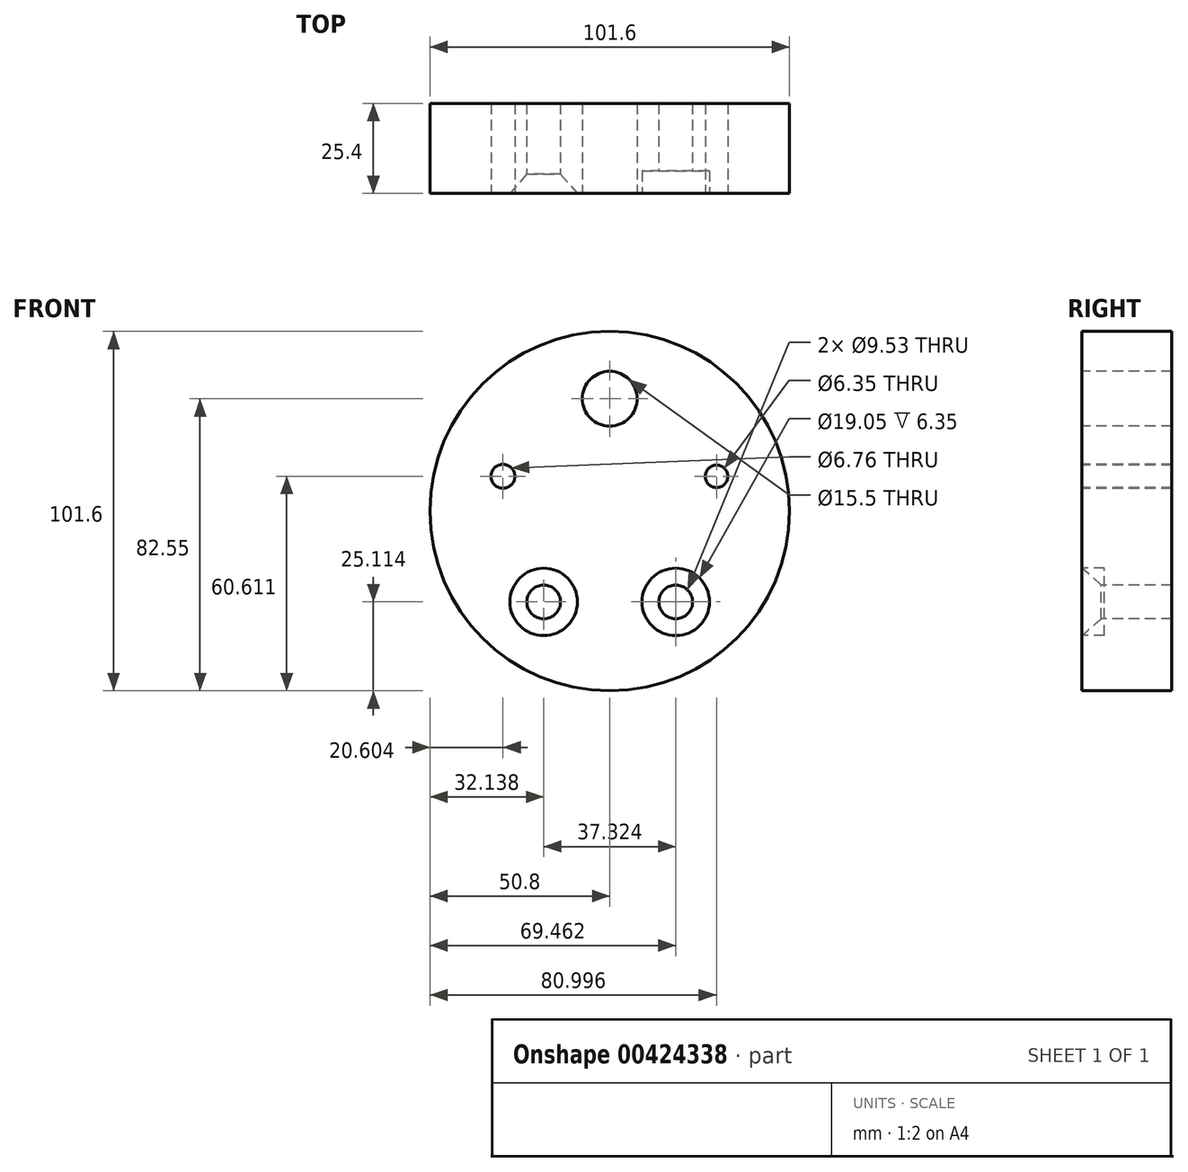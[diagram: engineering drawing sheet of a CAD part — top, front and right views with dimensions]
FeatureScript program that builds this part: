
annotation { "Feature Type Name" : "Feature", "Feature Type Description" : "" }
export const myFeature = defineFeature(function(context is Context, id is Id, definition is map)
    precondition{}
    {
        {
            var Q0;
            Q0=qCreatedBy(makeId("Front.planeOp"),FACE);
            var sketch = newSketch(context, id + "F0", { "sketchPlane" : qUnion([Q0])});
            skCircle(sketch, "E0", {"center": v(0, 0) * mm, "radius": 50.8 * mm});
            skSolve(sketch);
        }
        {
            var Q0;
            Q0=makeQuery(id+"F0.imprint","IMPRINT",FACE,{"disambiguationData":[TD([[makeQuery(id+"F0.imprint","IMPRINT",EDGE,{"derivedFrom":sQuery(id+"F0.wireOp",EDGE,"E0")}),1.0]])]});
            extrude(context, id + "F1", {"entities" : qUnion([Q0]), "depth" : 25.4 * mm});
        }
        {
            var Q0;
            Q0=makeQuery(id+"F1.opExtrude","CAP_FACE",FACE,{"disambiguationData":[OSD([sQuery(id+"F0.wireOp",EDGE,"E0")])],"isStart":false});
            var sketch = newSketch(context, id + "F2", { "sketchPlane" : qUnion([Q0])});
            skPoint(sketch, "E1", {"position": v(0, 31.75) * mm});
            skPoint(sketch, "E2.1.0", {"position": v(-30.2, 9.81) * mm});
            skPoint(sketch, "E2.2.0", {"position": v(-18.66, -25.69) * mm});
            skPoint(sketch, "E2.3.0", {"position": v(18.66, -25.69) * mm});
            skPoint(sketch, "E2.4.0", {"position": v(30.2, 9.81) * mm});
            skPoint(sketch, "E2.center", {"position": v(0, 0) * mm});
            skSolve(sketch);
        }
        {
            var Q0;
            Q0=sQuery(id+"F2.wireOp",VERTEX,"E2.4.0");
            var Q1;
            Q1=makeQuery(id+"F1.opExtrude","SWEPT_BODY",BODY,{"disambiguationData":[OSD([sQuery(id+"F0.wireOp",EDGE,"E0")])]});
            hole(context, id + "F3", {"style" : HoleStyle.SIMPLE, "endStyle" : HoleEndStyle.THROUGH, "holeDiameter" : 6.35 * mm, "isTappedThrough" : true, "tappedDepth" : 12.7 * mm, "tapClearance" : 3, "locations" : qUnion([Q0]), "scope" : qUnion([Q1])});
        }
        {
            var Q0;
            Q0=sQuery(id+"F2.wireOp",VERTEX,"E2.3.0");
            var Q1;
            Q1=makeQuery(id+"F1.opExtrude","SWEPT_BODY",BODY,{"disambiguationData":[OSD([sQuery(id+"F0.wireOp",EDGE,"E0")])]});
            hole(context, id + "F4", {"style" : HoleStyle.C_BORE, "endStyle" : HoleEndStyle.THROUGH, "holeDiameter" : 9.52 * mm, "cBoreDiameter" : 19.05 * mm, "cBoreDepth" : 6.35 * mm, "isTappedThrough" : true, "tappedDepth" : 12.7 * mm, "tapClearance" : 3, "locations" : qUnion([Q0]), "scope" : qUnion([Q1])});
        }
        {
            var Q0;
            Q0=sQuery(id+"F2.wireOp",VERTEX,"E2.2.0");
            var Q1;
            Q1=makeQuery(id+"F1.opExtrude","SWEPT_BODY",BODY,{"disambiguationData":[OSD([sQuery(id+"F0.wireOp",EDGE,"E0")])]});
            hole(context, id + "F5", {"style" : HoleStyle.C_SINK, "endStyle" : HoleEndStyle.THROUGH, "holeDiameter" : 9.52 * mm, "cSinkDiameter" : 19.05 * mm, "cSinkAngle" : 82 * degree, "isTappedThrough" : true, "tappedDepth" : 12.7 * mm, "tapClearance" : 3, "locations" : qUnion([Q0]), "scope" : qUnion([Q1])});
        }
        {
            var Q0;
            Q0=sQuery(id+"F2.wireOp",VERTEX,"E2.1.0");
            var Q1;
            Q1=makeQuery(id+"F1.opExtrude","SWEPT_BODY",BODY,{"disambiguationData":[OSD([sQuery(id+"F0.wireOp",EDGE,"E0")])]});
            hole(context, id + "F6", {"style" : HoleStyle.SIMPLE, "endStyle" : HoleEndStyle.THROUGH, "standardTappedOrClearance" : lookupTablePath({ "standard" : "ANSI", "fit" : "Normal (ASME)", "size" : "1/4", "type" : "Clearance" }), "standardBlindInLast" : lookupTablePath({ "fit" : "Free", "standard" : "ANSI", "size" : "1/4", "type" : "Clearance" }), "holeDiameter" : 6.76 * mm, "isTappedThrough" : true, "tappedDepth" : 12.7 * mm, "tapClearance" : 3, "locations" : qUnion([Q0]), "scope" : qUnion([Q1])});
        }
        {
            var Q0;
            Q0=sQuery(id+"F2.wireOp",VERTEX,"E1");
            var Q1;
            Q1=makeQuery(id+"F1.opExtrude","SWEPT_BODY",BODY,{"disambiguationData":[OSD([sQuery(id+"F0.wireOp",EDGE,"E0")])]});
            hole(context, id + "F7", {"style" : HoleStyle.SIMPLE, "endStyle" : HoleEndStyle.THROUGH, "standardTappedOrClearance" : lookupTablePath({ "standard" : "ISO", "fit" : "Normal", "size" : "M14", "type" : "Clearance" }), "standardBlindInLast" : lookupTablePath({ "fit" : "Standard", "standard" : "ISO", "size" : "M14", "type" : "Clearance" }), "holeDiameter" : 15.5 * mm, "isTappedThrough" : true, "tappedDepth" : 12.7 * mm, "tapClearance" : 3, "locations" : qUnion([Q0]), "scope" : qUnion([Q1])});
        }
    });
